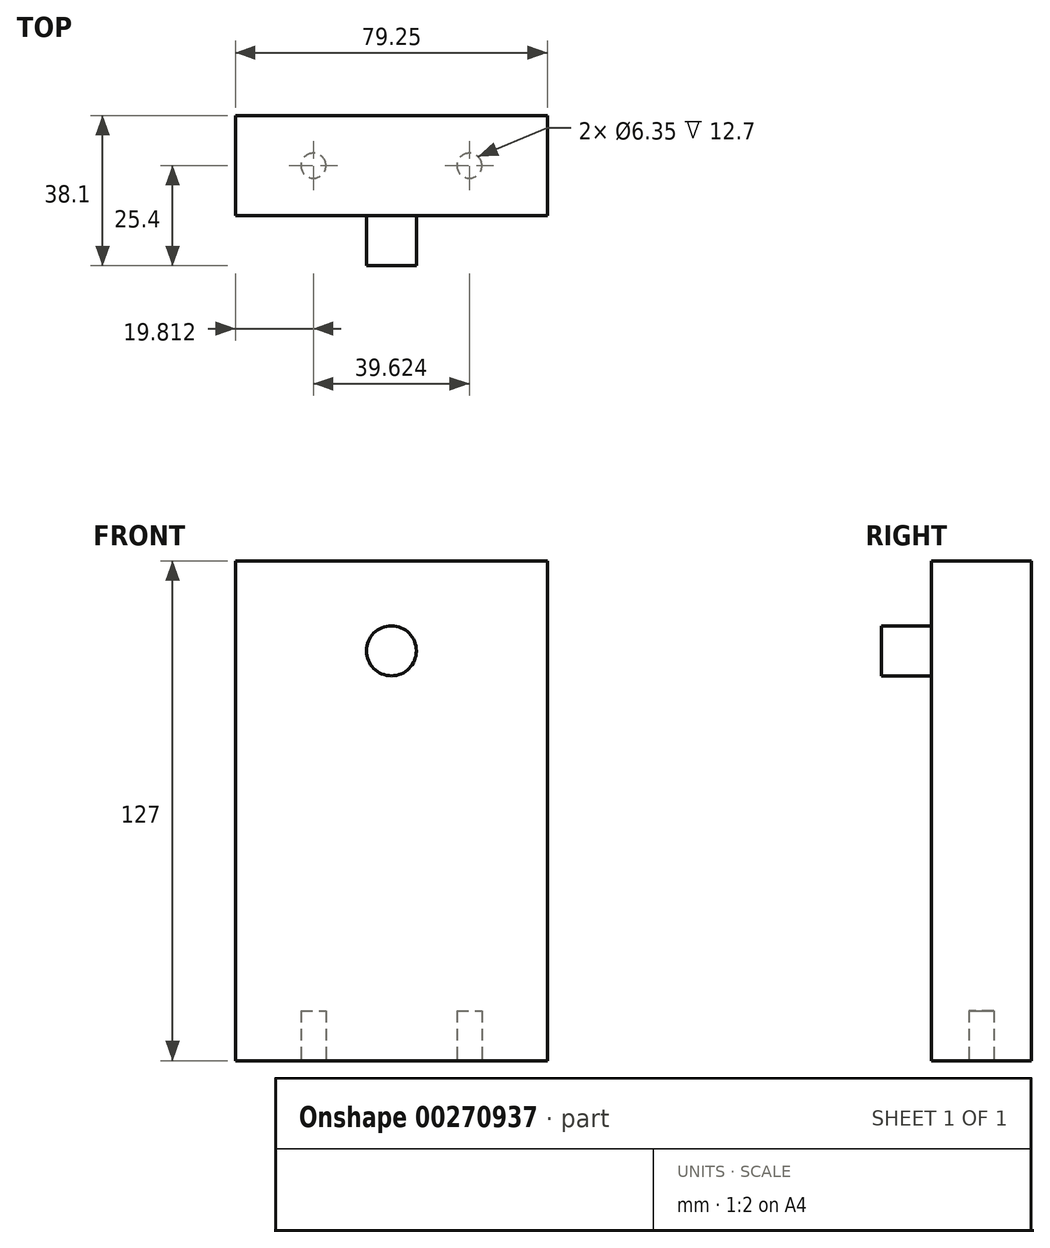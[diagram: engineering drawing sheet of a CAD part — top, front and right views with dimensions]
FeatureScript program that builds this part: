
annotation { "Feature Type Name" : "Feature", "Feature Type Description" : "" }
export const myFeature = defineFeature(function(context is Context, id is Id, definition is map)
    precondition{}
    {
        {
            var Q0;
            Q0=qCreatedBy(makeId("Front.planeOp"),FACE);
            var sketch = newSketch(context, id + "F0", { "sketchPlane" : qUnion([Q0])});
            skLineSegment(sketch, "E0", {"start": v(19.05, 127) * mm, "end": v(69.85, 127) * mm});
            skLineSegment(sketch, "E1", {"start": v(0, 0) * mm, "end": v(79.25, 0) * mm});
            skLineSegment(sketch, "E2", {"start": v(0, 0) * mm, "end": v(44.45, 0) * mm});
            skPoint(sketch, "E3.orphan", {"position": v(88.9, 0) * mm});
            skLineSegment(sketch, "E4", {"start": v(79.25, 0) * mm, "end": v(79.25, 127) * mm});
            skLineSegment(sketch, "E5", {"start": v(0, 0) * mm, "end": v(0, 127) * mm});
            skLineSegment(sketch, "E6", {"start": v(19.05, 127) * mm, "end": v(0, 127) * mm});
            skLineSegment(sketch, "E7", {"start": v(69.85, 127) * mm, "end": v(79.25, 127) * mm});
            skLineSegment(sketch, "E8", {"start": v(39.62, 0) * mm, "end": v(39.62, 111.13) * mm});
            skSolve(sketch);
        }
        {
            var Q0;
            Q0=makeQuery(id+"F0.imprint","IMPRINT",FACE,{"disambiguationData":[TD([[makeQuery(id+"F0.imprint","IMPRINT",EDGE,{"derivedFrom":sQuery(id+"F0.wireOp",EDGE,"E0")}),-1.0]])]});
            extrude(context, id + "F1", {"entities" : qUnion([Q0]), "depth" : 25.4 * mm});
        }
        {
            var Q0;
            Q0=makeQuery(id+"F1.opExtrude","CAP_FACE",FACE,{"disambiguationData":[OSD([sQuery(id+"F0.wireOp",EDGE,"E0"),sQuery(id+"F0.wireOp",EDGE,"E1"),sQuery(id+"F0.wireOp",EDGE,"E4"),sQuery(id+"F0.wireOp",EDGE,"E5"),sQuery(id+"F0.wireOp",EDGE,"E6"),sQuery(id+"F0.wireOp",EDGE,"E7")])],"isStart":false});
            var sketch = newSketch(context, id + "F2", { "sketchPlane" : qUnion([Q0])});
            skLineSegment(sketch, "E9", {"start": v(39.62, 0) * mm, "end": v(39.62, 104.14) * mm});
            skCircle(sketch, "E10", {"center": v(39.62, 104.14) * mm, "radius": 6.35 * mm});
            skSolve(sketch);
        }
        {
            var Q0;
            Q0 = qSketchRegion(id + "F2", true);
            extrude(context, id + "F3", {"entities" : qUnion([Q0]), "operationType" : NewBodyOperationType.ADD, "depth" : 12.7 * mm});
        }
        {
            var Q0;
            Q0=makeQuery(id+"F1.opExtrude","SWEPT_FACE",FACE,{"disambiguationData":[OSD([sQuery(id+"F0.wireOp",EDGE,"E1")])]});
            var sketch = newSketch(context, id + "F4", { "sketchPlane" : qUnion([Q0])});
            skLineSegment(sketch, "E11", {"start": v(0, 12.7) * mm, "end": v(79.25, 12.7) * mm});
            skLineSegment(sketch, "E12", {"start": v(39.62, 0) * mm, "end": v(39.62, 12.7) * mm});
            skLineSegment(sketch, "E13", {"start": v(39.62, 12.7) * mm, "end": v(59.44, 12.7) * mm});
            skLineSegment(sketch, "E14", {"start": v(39.62, 12.7) * mm, "end": v(19.81, 12.7) * mm});
            skCircle(sketch, "E15", {"center": v(19.81, 12.7) * mm, "radius": 3.18 * mm});
            skCircle(sketch, "E16", {"center": v(59.44, 12.7) * mm, "radius": 3.18 * mm});
            skSolve(sketch);
        }
        {
            var Q0;
            Q0 = qSketchRegion(id + "F4", true);
            extrude(context, id + "F5", {"entities" : qUnion([Q0]), "operationType" : NewBodyOperationType.REMOVE, "oppositeDirection" : true, "depth" : 12.7 * mm});
        }
    });
